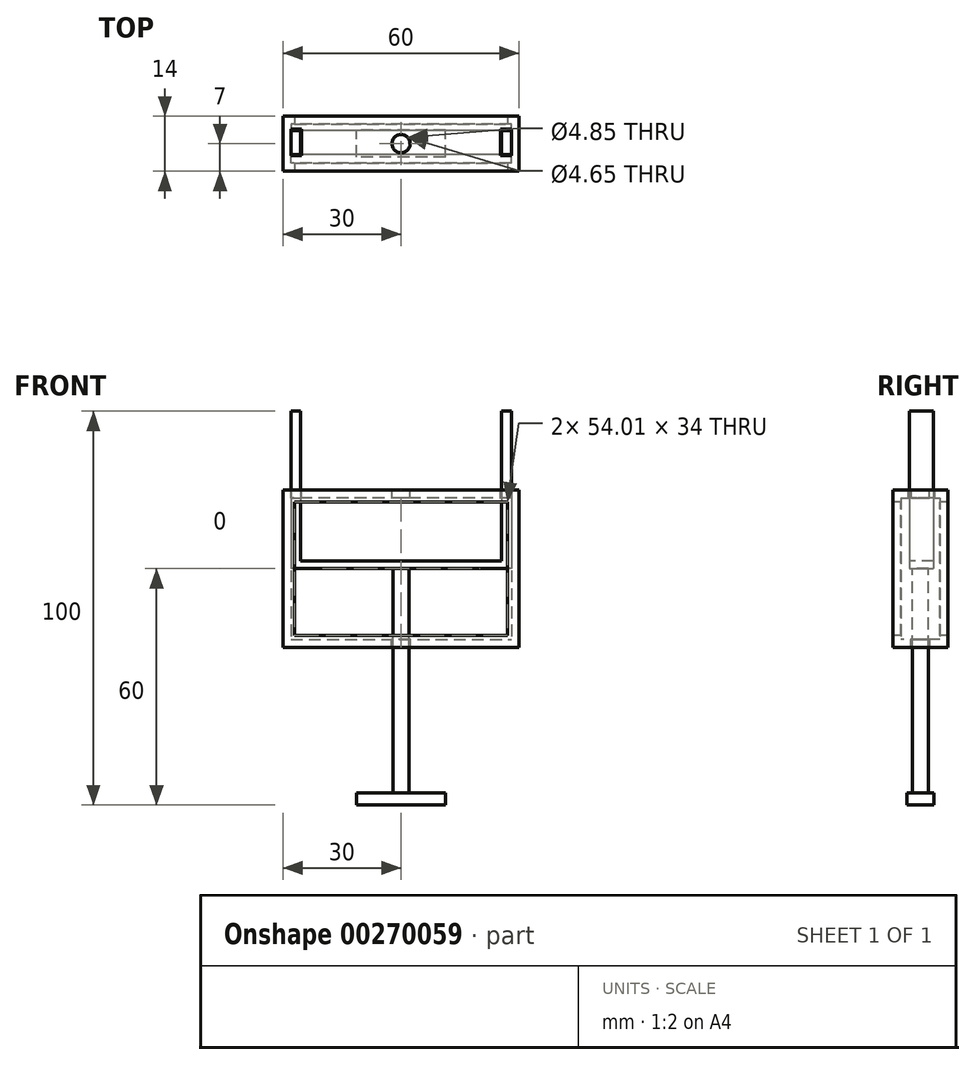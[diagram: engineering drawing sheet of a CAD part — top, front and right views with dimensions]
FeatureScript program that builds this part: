
annotation { "Feature Type Name" : "Feature", "Feature Type Description" : "" }
export const myFeature = defineFeature(function(context is Context, id is Id, definition is map)
    precondition{}
    {
        {
            var Q0;
            Q0=qCreatedBy(makeId("Top.planeOp"),FACE);
            var sketch = newSketch(context, id + "F0", { "sketchPlane" : qUnion([Q0])});
            skLineSegment(sketch, "E0.bottom", {"start": v(30, -7) * mm, "end": v(-30, -7) * mm});
            skLineSegment(sketch, "E0.top", {"start": v(30, 7) * mm, "end": v(-30, 7) * mm});
            skLineSegment(sketch, "E0.left", {"start": v(30, -7) * mm, "end": v(30, 7) * mm});
            skLineSegment(sketch, "E0.right", {"start": v(-30, -7) * mm, "end": v(-30, 7) * mm});
            skPoint(sketch, "E0.middle", {"position": v(0, 0) * mm});
            skLineSegment(sketch, "E1.bottom", {"start": v(7.56, -1.5) * mm, "end": v(-7.56, -1.5) * mm});
            skLineSegment(sketch, "E1.top", {"start": v(7.56, 1.5) * mm, "end": v(-7.56, 1.5) * mm});
            skLineSegment(sketch, "E1.left", {"start": v(7.56, -1.5) * mm, "end": v(7.56, 1.5) * mm});
            skLineSegment(sketch, "E1.right", {"start": v(-7.56, -1.5) * mm, "end": v(-7.56, 1.5) * mm});
            skLineSegment(sketch, "E2.0", {"start": v(8.56, 2.5) * mm, "end": v(-8.56, 2.5) * mm});
            skLineSegment(sketch, "E2.1", {"start": v(8.56, -2.5) * mm, "end": v(8.56, 2.5) * mm});
            skLineSegment(sketch, "E2.2", {"start": v(8.56, -2.5) * mm, "end": v(-8.56, -2.5) * mm});
            skLineSegment(sketch, "E2.3", {"start": v(-8.56, -2.5) * mm, "end": v(-8.56, 2.5) * mm});
            skLineSegment(sketch, "E3.0", {"start": v(28, 5) * mm, "end": v(-28, 5) * mm});
            skLineSegment(sketch, "E3.1", {"start": v(28, -5) * mm, "end": v(28, 5) * mm});
            skLineSegment(sketch, "E3.2", {"start": v(28, -5) * mm, "end": v(-28, -5) * mm});
            skLineSegment(sketch, "E3.3", {"start": v(-28, -5) * mm, "end": v(-28, 5) * mm});
            skLineSegment(sketch, "E4.0", {"start": v(33, -5) * mm, "end": v(33, 12.36) * mm});
            skLineSegment(sketch, "E5.0", {"start": v(27, 4) * mm, "end": v(-27, 4) * mm});
            skLineSegment(sketch, "E5.1", {"start": v(27, -4) * mm, "end": v(27, 4) * mm});
            skLineSegment(sketch, "E5.2", {"start": v(27, -4) * mm, "end": v(-27, -4) * mm});
            skLineSegment(sketch, "E5.3", {"start": v(-27, -4) * mm, "end": v(-27, 4) * mm});
            skSolve(sketch);
        }
        {
            var Q0;
            Q0 = qSketchRegion(id + "F0", true);
            var Q1;
            Q1=makeQuery(id+"F0.imprint","IMPRINT",FACE,{"disambiguationData":[TD([[makeQuery(id+"F0.imprint","IMPRINT",EDGE,{"derivedFrom":sQuery(id+"F0.wireOp",EDGE,"E2.0")}),-1.0]])]});
            var Q2;
            Q2=makeQuery(id+"F0.imprint","IMPRINT",FACE,{"disambiguationData":[TD([[makeQuery(id+"F0.imprint","IMPRINT",EDGE,{"derivedFrom":sQuery(id+"F0.wireOp",EDGE,"E3.0")}),1.0]])]});
            extrude(context, id + "F1", {"entities" : qUnion([Q0, Q1, Q2]), "depth" : 2 * mm});
        }
        {
            var Q0;
            Q0=makeQuery(id+"F0.imprint","IMPRINT",FACE,{"disambiguationData":[TD([[makeQuery(id+"F0.imprint","IMPRINT",EDGE,{"derivedFrom":sQuery(id+"F0.wireOp",EDGE,"E0.bottom")}),-1.0]])]});
            extrude(context, id + "F2", {"entities" : qUnion([Q0]), "operationType" : NewBodyOperationType.ADD, "depth" : 40 * mm});
        }
        {
            var Q0;
            {var subQ0=sQuery(id+"F0.wireOp",EDGE,"E0.bottom");Q0=makeQuery(id+"F2.boolean.opBoolean","MERGE",FACE,{"derivedFrom":[makeQuery(id+"F1.opExtrude","SWEPT_FACE",FACE,{"disambiguationData":[OSD([subQ0])]}),makeQuery(id+"F2.opExtrude","SWEPT_FACE",FACE,{"disambiguationData":[OSD([subQ0])]})]});}
            var sketch = newSketch(context, id + "F3", { "sketchPlane" : qUnion([Q0])});
            skLineSegment(sketch, "E6.bottom", {"start": v(-30, 0) * mm, "end": v(30, 0) * mm});
            skLineSegment(sketch, "E6.top", {"start": v(-30, 40) * mm, "end": v(30, 40) * mm});
            skLineSegment(sketch, "E6.left", {"start": v(-30, 0) * mm, "end": v(-30, 40) * mm});
            skLineSegment(sketch, "E6.right", {"start": v(30, 0) * mm, "end": v(30, 40) * mm});
            skLineSegment(sketch, "E7.0", {"start": v(-27, 3) * mm, "end": v(-27, 37) * mm});
            skLineSegment(sketch, "E7.1", {"start": v(-27, 3) * mm, "end": v(27, 3) * mm});
            skLineSegment(sketch, "E7.2", {"start": v(27, 3) * mm, "end": v(27, 37) * mm});
            skLineSegment(sketch, "E7.3", {"start": v(-27, 37) * mm, "end": v(27, 37) * mm});
            skLineSegment(sketch, "E8.0", {"start": v(-104.88, -74.87) * mm, "end": v(104.88, -74.87) * mm});
            skLineSegment(sketch, "E8.1", {"start": v(-104.88, 114.87) * mm, "end": v(-104.88, -74.87) * mm});
            skLineSegment(sketch, "E8.2", {"start": v(104.88, 114.87) * mm, "end": v(-104.88, 114.87) * mm});
            skLineSegment(sketch, "E8.3", {"start": v(104.88, -74.87) * mm, "end": v(104.88, 114.87) * mm});
            skSolve(sketch);
        }
        {
            var Q0;
            Q0=makeQuery(id+"F3.imprint","IMPRINT",FACE,{"disambiguationData":[TD([[makeQuery(id+"F3.imprint","IMPRINT",EDGE,{"derivedFrom":sQuery(id+"F3.wireOp",EDGE,"E7.0")}),-1.0]])]});
            extrude(context, id + "F4", {"entities" : qUnion([Q0]), "operationType" : NewBodyOperationType.REMOVE, "oppositeDirection" : true, "depth" : 25 * mm});
        }
        {
            var Q0;
            Q0=makeQuery(id+"F1.opExtrude","CAP_FACE",FACE,{"disambiguationData":[OSD([sQuery(id+"F0.wireOp",EDGE,"E0.bottom"),sQuery(id+"F0.wireOp",EDGE,"E0.top"),sQuery(id+"F0.wireOp",EDGE,"E0.left"),sQuery(id+"F0.wireOp",EDGE,"E0.right"),sQuery(id+"F0.wireOp",EDGE,"E2.0"),sQuery(id+"F0.wireOp",EDGE,"E2.1"),sQuery(id+"F0.wireOp",EDGE,"E2.2"),sQuery(id+"F0.wireOp",EDGE,"E2.3")])],"isStart":false});
            var sketch = newSketch(context, id + "F5", { "sketchPlane" : qUnion([Q0])});
            skLineSegment(sketch, "E9.bottom", {"start": v(-11, 4.94) * mm, "end": v(11, 4.94) * mm});
            skLineSegment(sketch, "E9.top", {"start": v(-11, -4.94) * mm, "end": v(11, -4.94) * mm});
            skLineSegment(sketch, "E9.left", {"start": v(-11, 4.94) * mm, "end": v(-11, -4.94) * mm});
            skLineSegment(sketch, "E9.right", {"start": v(11, 4.94) * mm, "end": v(11, -4.94) * mm});
            skPoint(sketch, "E9.middle", {"position": v(0, 0) * mm});
            skCircle(sketch, "E10", {"center": v(0, 0) * mm, "radius": 2.02 * mm});
            skCircle(sketch, "E11.0", {"center": v(0, 0) * mm, "radius": 2.42 * mm});
            skSolve(sketch);
        }
        {
            var Q0;
            Q0=makeQuery(id+"F5.imprint","IMPRINT",FACE,{"disambiguationData":[TD([[makeQuery(id+"F5.imprint","IMPRINT",EDGE,{"derivedFrom":sQuery(id+"F5.wireOp",EDGE,"E9.bottom")}),-1.0]])]});
            var Q1;
            Q1=makeQuery(id+"F5.imprint","IMPRINT",FACE,{"disambiguationData":[TD([[makeQuery(id+"F5.imprint","IMPRINT",EDGE,{"derivedFrom":sQuery(id+"F5.wireOp",EDGE,"E11.0")}),-1.0]])]});
            extrude(context, id + "F6", {"entities" : qUnion([Q0, Q1]), "operationType" : NewBodyOperationType.ADD, "oppositeDirection" : true, "depth" : 2 * mm});
        }
        {
            var Q0;
            Q0=makeQuery(id+"F2.opExtrude","CAP_FACE",FACE,{"disambiguationData":[OSD([sQuery(id+"F0.wireOp",EDGE,"E0.bottom"),sQuery(id+"F0.wireOp",EDGE,"E0.top"),sQuery(id+"F0.wireOp",EDGE,"E0.left"),sQuery(id+"F0.wireOp",EDGE,"E0.right"),sQuery(id+"F0.wireOp",EDGE,"E3.0"),sQuery(id+"F0.wireOp",EDGE,"E3.1"),sQuery(id+"F0.wireOp",EDGE,"E3.2"),sQuery(id+"F0.wireOp",EDGE,"E3.3")])],"isStart":false});
            var sketch = newSketch(context, id + "F7", { "sketchPlane" : qUnion([Q0])});
            skCircle(sketch, "E12", {"center": v(0, 0) * mm, "radius": 2.02 * mm});
            skLineSegment(sketch, "E13.bottom", {"start": v(28, 3.34) * mm, "end": v(25.58, 3.34) * mm});
            skLineSegment(sketch, "E13.top", {"start": v(28, -2.75) * mm, "end": v(25.58, -2.75) * mm});
            skLineSegment(sketch, "E13.left", {"start": v(28, 3.34) * mm, "end": v(28, -2.75) * mm});
            skLineSegment(sketch, "E13.right", {"start": v(25.58, 3.34) * mm, "end": v(25.58, -2.75) * mm});
            skLineSegment(sketch, "E14.MirrorCS", {"start": v(-28, 3.34) * mm, "end": v(-25.58, 3.34) * mm});
            skLineSegment(sketch, "E15.MirrorCS", {"start": v(-25.58, 3.34) * mm, "end": v(-25.58, -2.75) * mm});
            skLineSegment(sketch, "E16.MirrorCS", {"start": v(-28, -2.75) * mm, "end": v(-25.58, -2.75) * mm});
            skLineSegment(sketch, "E17.MirrorCS", {"start": v(-28, 3.34) * mm, "end": v(-28, -2.75) * mm});
            skLineSegment(sketch, "E18.0", {"start": v(28, 3.64) * mm, "end": v(25.28, 3.64) * mm});
            skLineSegment(sketch, "E18.1", {"start": v(25.28, 3.64) * mm, "end": v(25.28, -3.05) * mm});
            skLineSegment(sketch, "E18.2", {"start": v(28, -3.05) * mm, "end": v(25.28, -3.05) * mm});
            skLineSegment(sketch, "E19.0", {"start": v(-28, 3.64) * mm, "end": v(-25.28, 3.64) * mm});
            skLineSegment(sketch, "E19.1", {"start": v(-25.28, 3.64) * mm, "end": v(-25.28, -3.05) * mm});
            skLineSegment(sketch, "E19.2", {"start": v(-28, -3.05) * mm, "end": v(-25.28, -3.05) * mm});
            skCircle(sketch, "E20.0", {"center": v(0, 0) * mm, "radius": 2.32 * mm});
            skSolve(sketch);
        }
        {
            var Q0;
            Q0=makeQuery(id+"F7.imprint","IMPRINT",FACE,{"disambiguationData":[TD([[makeQuery(id+"F7.imprint","IMPRINT",EDGE,{"derivedFrom":makeQuery(id+"F2.opExtrude","CAP_EDGE",EDGE,{"disambiguationData":[OSD([sQuery(id+"F0.wireOp",EDGE,"E0.bottom")])],"isStart":false})}),-1.0]])]});
            var Q1;
            {var subQ2=sQuery(id+"F7.wireOp",EDGE,"E18.0");Q1=makeQuery(id+"F7.imprint","IMPRINT",FACE,{"disambiguationData":[TD([[makeQuery(id+"F7.imprint","IMPRINT",EDGE,{"derivedFrom":subQ2}),-1.0]])]});}
            extrude(context, id + "F8", {"entities" : qUnion([Q0, Q1]), "operationType" : NewBodyOperationType.ADD, "oppositeDirection" : true, "depth" : 2 * mm});
        }
        {
            var Q0;
            Q0=makeQuery(id+"F7.imprint","IMPRINT",FACE,{"disambiguationData":[TD([[makeQuery(id+"F7.imprint","IMPRINT",EDGE,{"derivedFrom":sQuery(id+"F7.wireOp",EDGE,"E13.bottom")}),1.0]])]});
            var Q1;
            Q1=makeQuery(id+"F7.imprint","IMPRINT",FACE,{"disambiguationData":[TD([[makeQuery(id+"F7.imprint","IMPRINT",EDGE,{"derivedFrom":sQuery(id+"F7.wireOp",EDGE,"E14.MirrorCS")}),-1.0]])]});
            extrude(context, id + "F9", {"entities" : qUnion([Q0, Q1]), "endBound" : BoundingType.SYMMETRIC, "depth" : 40 * mm});
        }
        {
            var Q0;
            Q0=makeQuery(id+"F9.opExtrude","SWEPT_FACE",FACE,{"disambiguationData":[OSD([sQuery(id+"F7.wireOp",EDGE,"E15.MirrorCS")])]});
            var sketch = newSketch(context, id + "F10", { "sketchPlane" : qUnion([Q0])});
            skLineSegment(sketch, "E21.bottom", {"start": v(3.34, 20) * mm, "end": v(-2.75, 20) * mm});
            skLineSegment(sketch, "E21.top", {"start": v(3.34, 22) * mm, "end": v(-2.75, 22) * mm});
            skLineSegment(sketch, "E21.left", {"start": v(3.34, 20) * mm, "end": v(3.34, 22) * mm});
            skLineSegment(sketch, "E21.right", {"start": v(-2.75, 20) * mm, "end": v(-2.75, 22) * mm});
            skSolve(sketch);
        }
        {
            var Q0;
            Q0=makeQuery(id+"F10.imprint","IMPRINT",FACE,{"disambiguationData":[TD([[makeQuery(id+"F10.imprint","IMPRINT",EDGE,{"derivedFrom":sQuery(id+"F10.wireOp",EDGE,"E21.bottom")}),-1.0]])]});
            extrude(context, id + "F11", {"entities" : qUnion([Q0]), "operationType" : NewBodyOperationType.ADD, "endBound" : BoundingType.UP_TO_NEXT, "depth" : 25 * mm});
        }
        {
            var Q0;
            Q0=makeQuery(id+"F11.boolean.opBoolean","MERGE",FACE,{"derivedFrom":[makeQuery(id+"F9.opExtrude","CAP_FACE",FACE,{"disambiguationData":[OSD([sQuery(id+"F7.wireOp",EDGE,"E13.bottom"),sQuery(id+"F7.wireOp",EDGE,"E13.top"),sQuery(id+"F7.wireOp",EDGE,"E13.left"),sQuery(id+"F7.wireOp",EDGE,"E13.right")])],"isStart":true}),makeQuery(id+"F9.opExtrude","CAP_FACE",FACE,{"disambiguationData":[OSD([sQuery(id+"F7.wireOp",EDGE,"E14.MirrorCS"),sQuery(id+"F7.wireOp",EDGE,"E15.MirrorCS"),sQuery(id+"F7.wireOp",EDGE,"E16.MirrorCS"),sQuery(id+"F7.wireOp",EDGE,"E17.MirrorCS")])],"isStart":true}),makeQuery(id+"F11.opExtrude","SWEPT_FACE",FACE,{"disambiguationData":[OSD([sQuery(id+"F10.wireOp",EDGE,"E21.bottom")])]})]});
            var sketch = newSketch(context, id + "F12", { "sketchPlane" : qUnion([Q0])});
            skCircle(sketch, "E22", {"center": v(0, 0) * mm, "radius": 2.07 * mm});
            skSolve(sketch);
        }
        {
            var Q0;
            Q0 = qSketchRegion(id + "F12", true);
            extrude(context, id + "F13", {"entities" : qUnion([Q0]), "depth" : 60 * mm});
        }
        {
            var Q0;
            Q0=makeQuery(id+"F13.opExtrude","CAP_FACE",FACE,{"disambiguationData":[OSD([sQuery(id+"F12.wireOp",EDGE,"E22")])],"isStart":false});
            var sketch = newSketch(context, id + "F14", { "sketchPlane" : qUnion([Q0])});
            skLineSegment(sketch, "E23.bottom", {"start": v(11.3, 3.41) * mm, "end": v(-11.3, 3.41) * mm});
            skLineSegment(sketch, "E23.top", {"start": v(11.3, -3.41) * mm, "end": v(-11.3, -3.41) * mm});
            skLineSegment(sketch, "E23.left", {"start": v(11.3, 3.41) * mm, "end": v(11.3, -3.41) * mm});
            skLineSegment(sketch, "E23.right", {"start": v(-11.3, 3.41) * mm, "end": v(-11.3, -3.41) * mm});
            skPoint(sketch, "E23.middle", {"position": v(0, 0) * mm});
            skSolve(sketch);
        }
        {
            var Q0;
            Q0=makeQuery(id+"F14.imprint","IMPRINT",FACE,{"disambiguationData":[TD([[makeQuery(id+"F14.imprint","IMPRINT",EDGE,{"derivedFrom":sQuery(id+"F14.wireOp",EDGE,"E23.bottom")}),1.0]])]});
            extrude(context, id + "F15", {"entities" : qUnion([Q0]), "operationType" : NewBodyOperationType.ADD, "oppositeDirection" : true, "depth" : 3 * mm});
        }
    });
